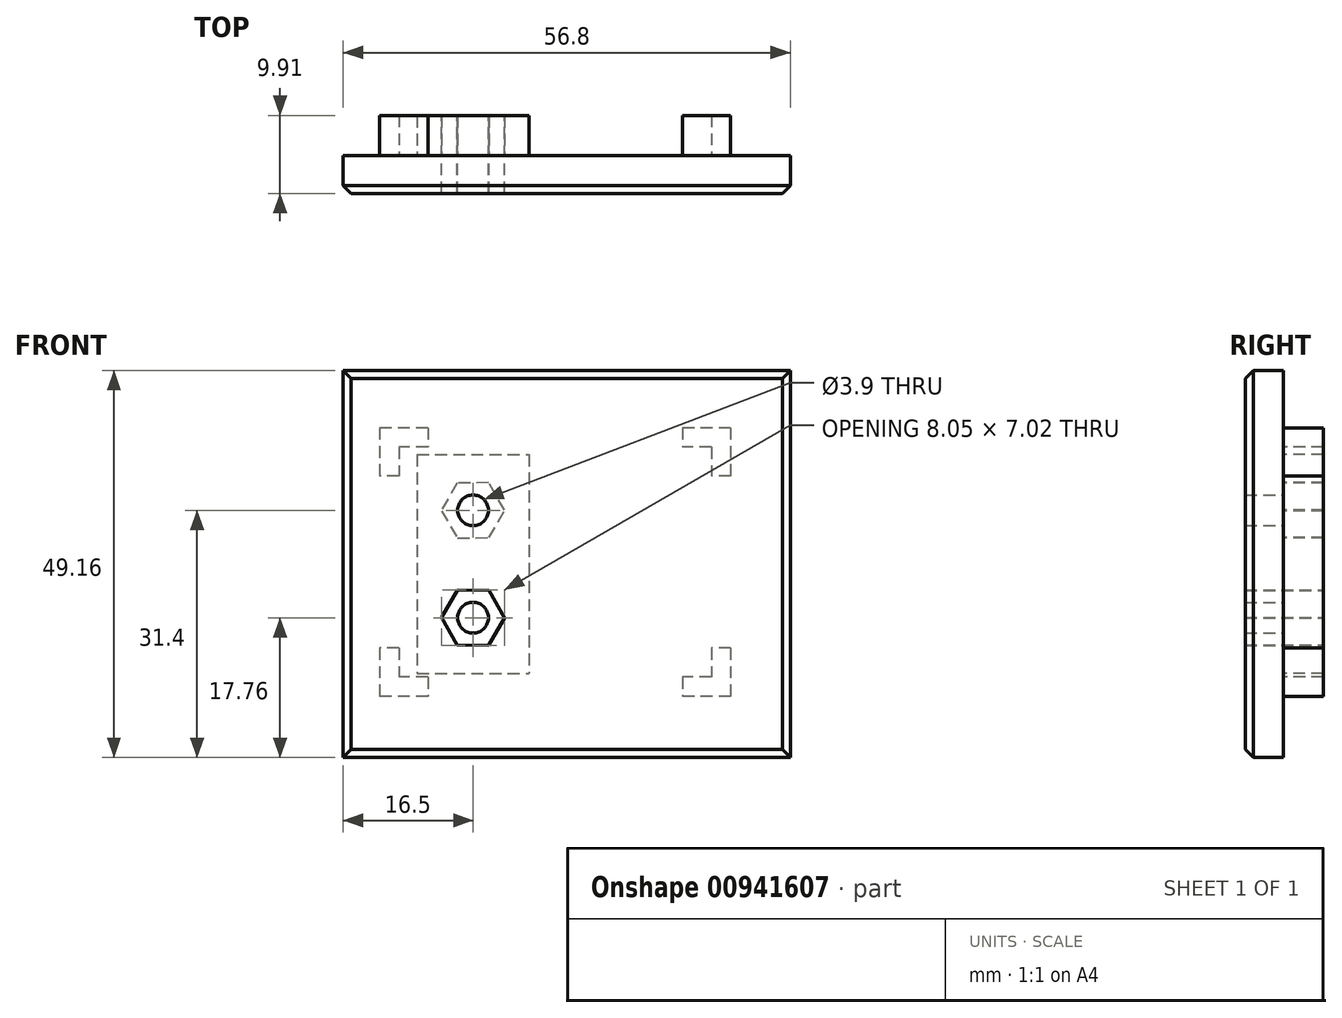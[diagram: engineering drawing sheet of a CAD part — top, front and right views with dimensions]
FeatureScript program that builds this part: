
annotation { "Feature Type Name" : "Feature", "Feature Type Description" : "" }
export const myFeature = defineFeature(function(context is Context, id is Id, definition is map)
    precondition{}
    {
        {
            var Q0;
            Q0=qCreatedBy(makeId("Front.planeOp"),FACE);
            var sketch = newSketch(context, id + "F0", { "sketchPlane" : qUnion([Q0])});
            skLineSegment(sketch, "E0.bottom", {"start": v(28.4, -24.58) * mm, "end": v(-28.4, -24.58) * mm});
            skLineSegment(sketch, "E0.top", {"start": v(28.4, 24.58) * mm, "end": v(-28.4, 24.58) * mm});
            skLineSegment(sketch, "E0.left", {"start": v(28.4, -24.58) * mm, "end": v(28.4, 24.58) * mm});
            skLineSegment(sketch, "E0.right", {"start": v(-28.4, -24.58) * mm, "end": v(-28.4, 24.58) * mm});
            skPoint(sketch, "E0.middle", {"position": v(0, 0) * mm});
            skSolve(sketch);
        }
        {
            var Q0;
            Q0 = qSketchRegion(id + "F0", true);
            extrude(context, id + "F1", {"entities" : qUnion([Q0]), "depth" : 4.83 * mm, "offsetDistance" : 25 * mm});
        }
        {
            var Q0;
            Q0=makeQuery(id+"F1.opExtrude","CAP_EDGE",EDGE,{"disambiguationData":[OSD([sQuery(id+"F0.wireOp",EDGE,"E0.left")])],"isStart":false});
            var Q1;
            Q1=makeQuery(id+"F1.opExtrude","CAP_EDGE",EDGE,{"disambiguationData":[OSD([sQuery(id+"F0.wireOp",EDGE,"E0.top")])],"isStart":false});
            var Q2;
            Q2=makeQuery(id+"F1.opExtrude","CAP_EDGE",EDGE,{"disambiguationData":[OSD([sQuery(id+"F0.wireOp",EDGE,"E0.right")])],"isStart":false});
            var Q3;
            Q3=makeQuery(id+"F1.opExtrude","CAP_EDGE",EDGE,{"disambiguationData":[OSD([sQuery(id+"F0.wireOp",EDGE,"E0.bottom")])],"isStart":false});
            chamfer(context, id + "F2", {"entities" : qUnion([Q0, Q1, Q2, Q3]), "width" : 1 * mm, "tangentPropagation" : true});
        }
        {
            var Q0;
            Q0=makeQuery(id+"F1.opExtrude","CAP_FACE",FACE,{"disambiguationData":[OSD([sQuery(id+"F0.wireOp",EDGE,"E0.bottom"),sQuery(id+"F0.wireOp",EDGE,"E0.top"),sQuery(id+"F0.wireOp",EDGE,"E0.left"),sQuery(id+"F0.wireOp",EDGE,"E0.right")])],"isStart":true});
            var sketch = newSketch(context, id + "F3", { "sketchPlane" : qUnion([Q0])});
            skLineSegment(sketch, "E1.bottom", {"start": v(-20.82, 17.29) * mm, "end": v(23.75, 17.29) * mm});
            skLineSegment(sketch, "E1.top", {"start": v(-20.82, -16.8) * mm, "end": v(23.75, -16.8) * mm});
            skLineSegment(sketch, "E1.left", {"start": v(-20.82, 17.29) * mm, "end": v(-20.82, -16.8) * mm});
            skLineSegment(sketch, "E1.right", {"start": v(23.75, 17.29) * mm, "end": v(23.75, -16.8) * mm});
            skLineSegment(sketch, "E2.0", {"start": v(-18.37, 14.84) * mm, "end": v(21.3, 14.84) * mm});
            skLineSegment(sketch, "E2.1", {"start": v(-18.37, 14.84) * mm, "end": v(-18.37, -14.35) * mm});
            skLineSegment(sketch, "E2.2", {"start": v(-18.37, -14.35) * mm, "end": v(21.3, -14.35) * mm});
            skLineSegment(sketch, "E2.3", {"start": v(21.3, 14.84) * mm, "end": v(21.3, -14.35) * mm});
            skLineSegment(sketch, "E3", {"start": v(-14.7, 17.29) * mm, "end": v(-14.7, 14.84) * mm});
            skLineSegment(sketch, "E4", {"start": v(-20.82, 11.18) * mm, "end": v(-18.37, 11.18) * mm});
            skLineSegment(sketch, "E5", {"start": v(-20.82, -10.7) * mm, "end": v(-18.37, -10.7) * mm});
            skLineSegment(sketch, "E6", {"start": v(-14.7, -14.35) * mm, "end": v(-14.7, -16.8) * mm});
            skLineSegment(sketch, "E7", {"start": v(17.64, -14.35) * mm, "end": v(17.64, -16.8) * mm});
            skLineSegment(sketch, "E8", {"start": v(21.3, -10.7) * mm, "end": v(23.75, -10.7) * mm});
            skLineSegment(sketch, "E9", {"start": v(21.3, 11.18) * mm, "end": v(23.75, 11.18) * mm});
            skLineSegment(sketch, "E10", {"start": v(17.64, 17.29) * mm, "end": v(17.64, 14.84) * mm});
            skSolve(sketch);
        }
        {
            var Q0;
            {var subQ3=sQuery(id+"F3.wireOp",EDGE,"E9");Q0=makeQuery(id+"F3.imprint","IMPRINT",FACE,{"disambiguationData":[TD([[makeQuery(id+"F3.imprint","IMPRINT",EDGE,{"derivedFrom":subQ3}),1.0]])]});}
            var Q1;
            {var subQ3=sQuery(id+"F3.wireOp",EDGE,"E5");Q1=makeQuery(id+"F3.imprint","IMPRINT",FACE,{"disambiguationData":[TD([[makeQuery(id+"F3.imprint","IMPRINT",EDGE,{"derivedFrom":subQ3}),-1.0]])]});}
            var Q2;
            {var subQ7=sQuery(id+"F3.wireOp",EDGE,"E7");Q2=makeQuery(id+"F3.imprint","IMPRINT",FACE,{"disambiguationData":[TD([[makeQuery(id+"F3.imprint","IMPRINT",EDGE,{"derivedFrom":subQ7}),1.0]])]});}
            var Q3;
            {var subQ3=sQuery(id+"F3.wireOp",EDGE,"E3");Q3=makeQuery(id+"F3.imprint","IMPRINT",FACE,{"disambiguationData":[TD([[makeQuery(id+"F3.imprint","IMPRINT",EDGE,{"derivedFrom":subQ3}),-1.0]])]});}
            extrude(context, id + "F4", {"entities" : qUnion([Q0, Q1, Q2, Q3]), "operationType" : NewBodyOperationType.ADD, "depth" : 5.08 * mm, "offsetDistance" : 25 * mm});
        }
        {
            var Q0;
            Q0=makeQuery(id+"F1.opExtrude","CAP_FACE",FACE,{"disambiguationData":[OSD([sQuery(id+"F0.wireOp",EDGE,"E0.bottom"),sQuery(id+"F0.wireOp",EDGE,"E0.top"),sQuery(id+"F0.wireOp",EDGE,"E0.left"),sQuery(id+"F0.wireOp",EDGE,"E0.right")])],"isStart":true});
            var sketch = newSketch(context, id + "F5", { "sketchPlane" : qUnion([Q0])});
            skLineSegment(sketch, "E11.bottom", {"start": v(19, 13.92) * mm, "end": v(4.8, 13.92) * mm});
            skLineSegment(sketch, "E11.top", {"start": v(19, -0.28) * mm, "end": v(4.8, -0.28) * mm});
            skLineSegment(sketch, "E11.left", {"start": v(19, 13.92) * mm, "end": v(19, -0.28) * mm});
            skLineSegment(sketch, "E11.right", {"start": v(4.8, 13.92) * mm, "end": v(4.8, -0.28) * mm});
            skPoint(sketch, "E11.middle", {"position": v(11.9, 6.82) * mm});
            skCircle(sketch, "E12.cCircle", {"center": v(11.9, 6.82) * mm, "radius": 3.48 * mm, "construction": true});
            skLineSegment(sketch, "E12.0", {"start": v(15.92, 6.77) * mm, "end": v(13.87, 3.3) * mm});
            skLineSegment(sketch, "E12.1", {"start": v(13.87, 3.3) * mm, "end": v(9.84, 3.36) * mm});
            skLineSegment(sketch, "E12.2", {"start": v(9.84, 3.36) * mm, "end": v(7.88, 6.87) * mm});
            skLineSegment(sketch, "E12.3", {"start": v(7.88, 6.87) * mm, "end": v(9.93, 10.33) * mm});
            skLineSegment(sketch, "E12.4", {"start": v(9.93, 10.33) * mm, "end": v(13.96, 10.28) * mm});
            skLineSegment(sketch, "E12.5", {"start": v(13.96, 10.28) * mm, "end": v(15.92, 6.77) * mm});
            skPoint(sketch, "E12.0.midPoint", {"position": v(14.9, 5.04) * mm});
            skCircle(sketch, "E13", {"center": v(11.9, 6.82) * mm, "radius": 1.95 * mm});
            skLineSegment(sketch, "E14.MirrorCS", {"start": v(19, -13.92) * mm, "end": v(19, 0.28) * mm});
            skLineSegment(sketch, "E15.MirrorCS", {"start": v(4.8, -13.92) * mm, "end": v(4.8, 0.28) * mm});
            skLineSegment(sketch, "E16.MirrorCS", {"start": v(19, -13.92) * mm, "end": v(4.8, -13.92) * mm});
            skCircle(sketch, "E17.MirrorC", {"center": v(11.9, -6.82) * mm, "radius": 3.48 * mm, "construction": true});
            skLineSegment(sketch, "E18.MirrorCS", {"start": v(7.88, -6.87) * mm, "end": v(9.93, -10.33) * mm});
            skLineSegment(sketch, "E19.MirrorCS", {"start": v(9.93, -10.33) * mm, "end": v(13.96, -10.28) * mm});
            skLineSegment(sketch, "E20.MirrorCS", {"start": v(13.96, -10.28) * mm, "end": v(15.92, -6.77) * mm});
            skLineSegment(sketch, "E21.MirrorCS", {"start": v(15.92, -6.77) * mm, "end": v(13.87, -3.3) * mm});
            skLineSegment(sketch, "E22.MirrorCS", {"start": v(13.87, -3.3) * mm, "end": v(9.84, -3.36) * mm});
            skLineSegment(sketch, "E23.MirrorCS", {"start": v(9.84, -3.36) * mm, "end": v(7.88, -6.87) * mm});
            skCircle(sketch, "E24.MirrorC", {"center": v(11.9, -6.82) * mm, "radius": 1.95 * mm});
            skSolve(sketch);
        }
        {
            var Q0;
            Q0=makeQuery(id+"F5.imprint","IMPRINT",FACE,{"disambiguationData":[TD([[makeQuery(id+"F5.imprint","IMPRINT",EDGE,{"derivedFrom":sQuery(id+"F5.wireOp",EDGE,"E13")}),1.0]])]});
            var Q1;
            Q1=makeQuery(id+"F5.imprint","IMPRINT",FACE,{"disambiguationData":[TD([[makeQuery(id+"F5.imprint","IMPRINT",EDGE,{"derivedFrom":sQuery(id+"F5.wireOp",EDGE,"E24.MirrorC")}),-1.0]])]});
            var Q2;
            Q2=sQuery(id+"F5.wireOp",EDGE,"E13");
            var Q3;
            Q3=sQuery(id+"F5.wireOp",EDGE,"E24.MirrorC");
            extrude(context, id + "F6", {"entities" : qUnion([Q0, Q1]), "operationType" : NewBodyOperationType.REMOVE, "surfaceEntities" : qUnion([Q2, Q3]), "oppositeDirection" : true, "depth" : 25 * mm, "offsetDistance" : 25 * mm});
        }
        {
            var Q0;
            Q0=makeQuery(id+"F5.imprint","IMPRINT",FACE,{"disambiguationData":[TD([[makeQuery(id+"F5.imprint","IMPRINT",EDGE,{"derivedFrom":sQuery(id+"F5.wireOp",EDGE,"E11.bottom")}),1.0]])]});
            var Q1;
            {var subQ2=sQuery(id+"F5.wireOp",EDGE,"E11.top");Q1=makeQuery(id+"F5.imprint","IMPRINT",FACE,{"disambiguationData":[TD([[makeQuery(id+"F5.imprint","IMPRINT",EDGE,{"derivedFrom":subQ2}),1.0]])]});}
            extrude(context, id + "F7", {"entities" : qUnion([Q0, Q1]), "operationType" : NewBodyOperationType.ADD, "depth" : 5.06 * mm, "offsetDistance" : 25 * mm});
        }
    });
